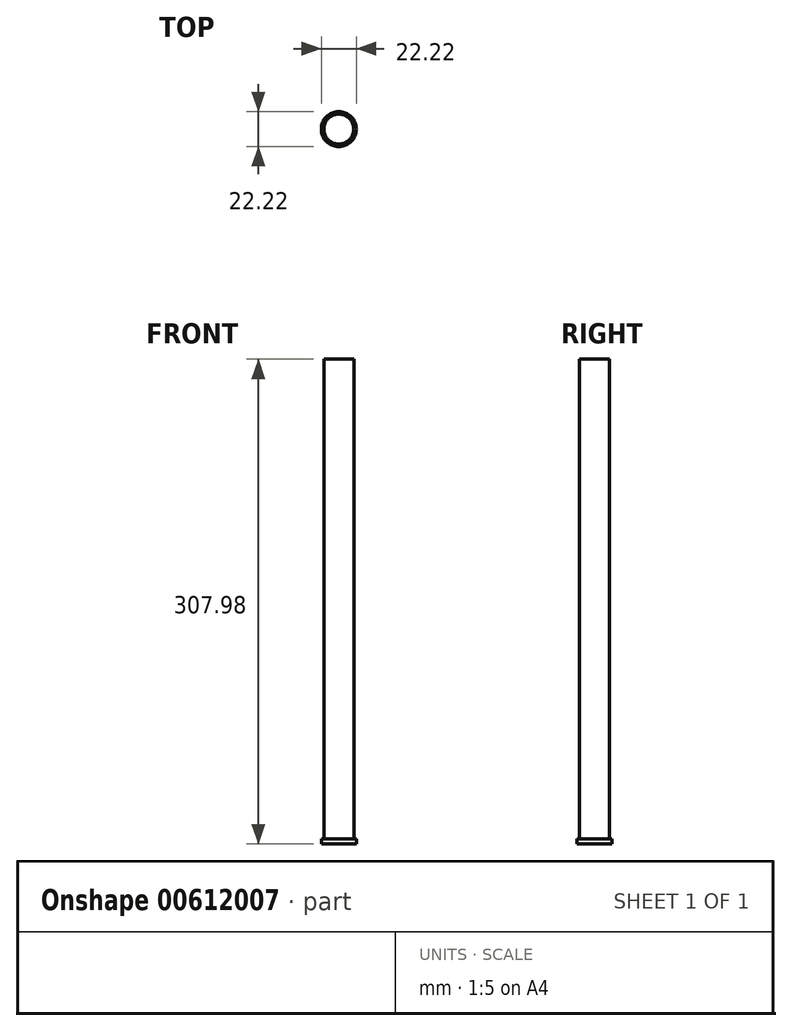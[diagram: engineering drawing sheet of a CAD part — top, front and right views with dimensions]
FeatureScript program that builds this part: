
annotation { "Feature Type Name" : "Feature", "Feature Type Description" : "" }
export const myFeature = defineFeature(function(context is Context, id is Id, definition is map)
    precondition{}
    {
        {
            var Q0;
            Q0=qCreatedBy(makeId("Top.planeOp"),FACE);
            var sketch = newSketch(context, id + "F0", { "sketchPlane" : qUnion([Q0])});
            skCircle(sketch, "E0", {"center": v(0, 0) * mm, "radius": 9.53 * mm});
            skPoint(sketch, "E1.center.orphan", {"position": v(-29.06, 0) * mm});
            skSolve(sketch);
        }
        {
            var Q0;
            Q0 = qSketchRegion(id + "F0", true);
            extrude(context, id + "F1", {"entities" : qUnion([Q0]), "depth" : 304.8 * mm, "offsetDistance" : 25 * mm});
        }
        {
            var Q0;
            Q0=qCreatedBy(makeId("Top.planeOp"),FACE);
            var sketch = newSketch(context, id + "F2", { "sketchPlane" : qUnion([Q0])});
            skCircle(sketch, "E2", {"center": v(0, 0) * mm, "radius": 11.11 * mm});
            skPoint(sketch, "E3.center.orphan", {"position": v(-17.87, 0) * mm});
            skSolve(sketch);
        }
        {
            var Q0;
            Q0 = qSketchRegion(id + "F2", true);
            extrude(context, id + "F3", {"entities" : qUnion([Q0]), "operationType" : NewBodyOperationType.ADD, "oppositeDirection" : true, "depth" : 3.17 * mm, "offsetDistance" : 25 * mm});
        }
    });
